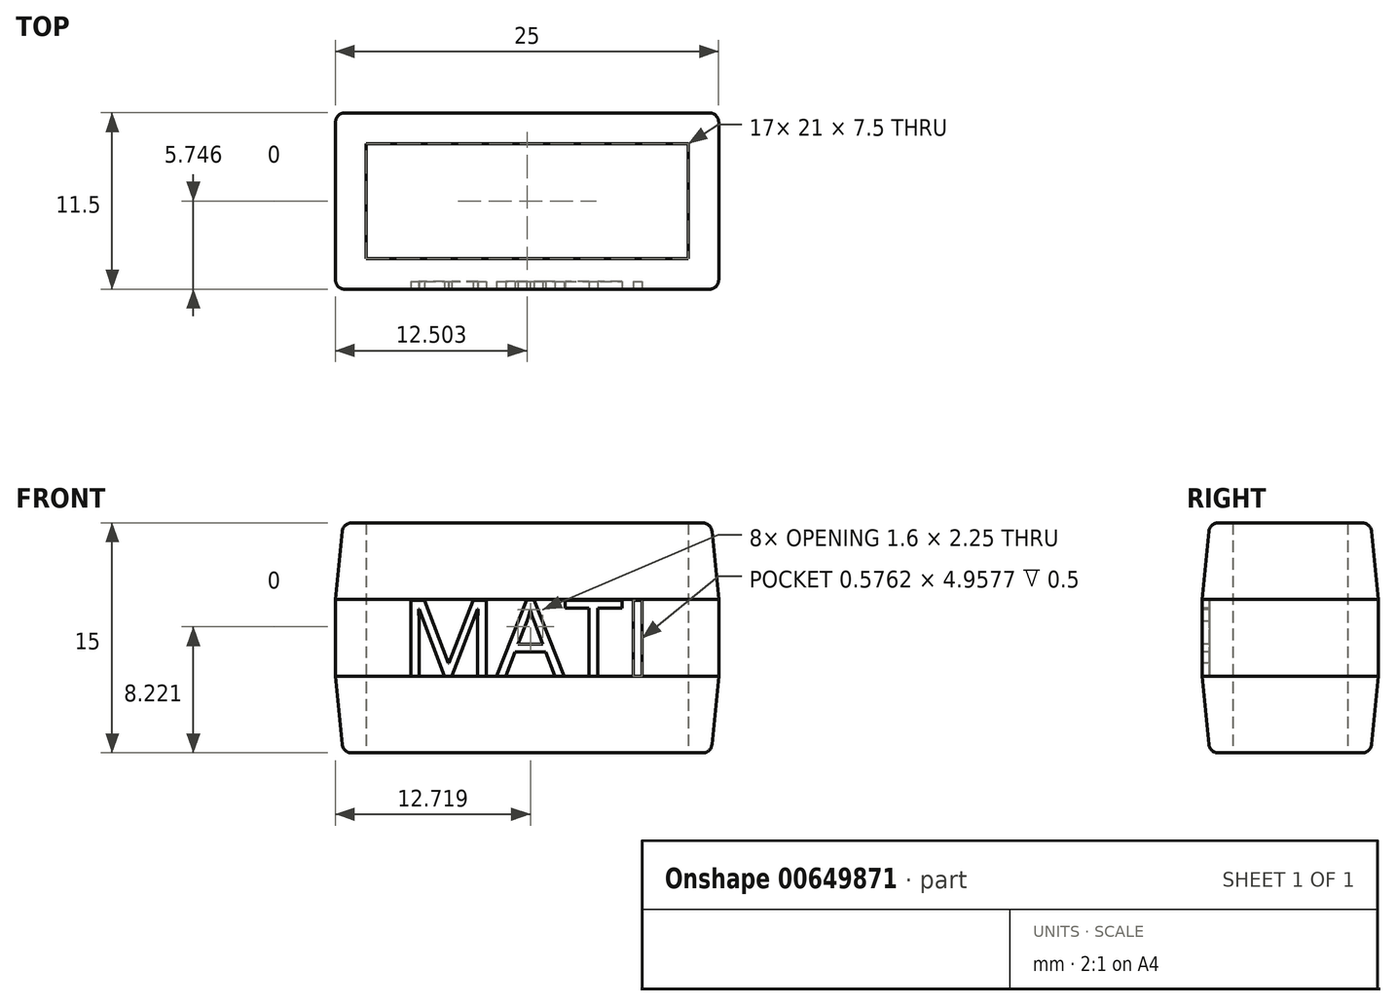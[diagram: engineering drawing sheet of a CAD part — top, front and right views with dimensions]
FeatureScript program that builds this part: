
annotation { "Feature Type Name" : "Feature", "Feature Type Description" : "" }
export const myFeature = defineFeature(function(context is Context, id is Id, definition is map)
    precondition{}
    {
        {
            var Q0;
            Q0=qCreatedBy(makeId("Top.planeOp"),FACE);
            var sketch = newSketch(context, id + "F0", { "sketchPlane" : qUnion([Q0])});
            skLineSegment(sketch, "E0.bottom", {"start": v(-10.05, 2.82) * mm, "end": v(10.95, 2.82) * mm});
            skLineSegment(sketch, "E0.top", {"start": v(-10.05, -4.68) * mm, "end": v(10.95, -4.68) * mm});
            skLineSegment(sketch, "E0.left", {"start": v(-10.05, 2.82) * mm, "end": v(-10.05, -4.68) * mm});
            skLineSegment(sketch, "E0.right", {"start": v(10.95, 2.82) * mm, "end": v(10.95, -4.68) * mm});
            skLineSegment(sketch, "E1", {"start": v(-19.72, 0) * mm, "end": v(20.77, 0) * mm, "construction": true});
            skLineSegment(sketch, "E2", {"start": v(0, 18.73) * mm, "end": v(0, -21.6) * mm, "construction": true});
            skLineSegment(sketch, "E3.0", {"start": v(-12.05, 4.82) * mm, "end": v(12.95, 4.82) * mm});
            skLineSegment(sketch, "E3.1", {"start": v(-12.05, 4.82) * mm, "end": v(-12.05, -6.68) * mm});
            skLineSegment(sketch, "E3.2", {"start": v(-12.05, -6.68) * mm, "end": v(12.95, -6.68) * mm});
            skLineSegment(sketch, "E3.3", {"start": v(12.95, 4.82) * mm, "end": v(12.95, -6.68) * mm});
            skSolve(sketch);
        }
        {
            var Q0;
            Q0=makeQuery(id+"F0.imprint","IMPRINT",FACE,{"disambiguationData":[TD([[makeQuery(id+"F0.imprint","IMPRINT",EDGE,{"derivedFrom":sQuery(id+"F0.wireOp",EDGE,"E0.bottom")}),1.0]])]});
            extrude(context, id + "F1", {"entities" : qUnion([Q0]), "depth" : 15 * mm, "offsetDistance" : 25 * mm});
        }
        {
            var Q0;
            Q0=makeQuery(id+"F1.opExtrude","CAP_EDGE",EDGE,{"disambiguationData":[OSD([sQuery(id+"F0.wireOp",EDGE,"E3.0")])],"isStart":false});
            var Q1;
            Q1=makeQuery(id+"F1.opExtrude","CAP_EDGE",EDGE,{"disambiguationData":[OSD([sQuery(id+"F0.wireOp",EDGE,"E3.3")])],"isStart":false});
            var Q2;
            Q2=makeQuery(id+"F1.opExtrude","CAP_EDGE",EDGE,{"disambiguationData":[OSD([sQuery(id+"F0.wireOp",EDGE,"E3.2")])],"isStart":false});
            var Q3;
            Q3=makeQuery(id+"F1.opExtrude","CAP_EDGE",EDGE,{"disambiguationData":[OSD([sQuery(id+"F0.wireOp",EDGE,"E3.1")])],"isStart":false});
            chamfer(context, id + "F2", {"entities" : qUnion([Q0, Q1, Q2, Q3]), "chamferType" : ChamferType.TWO_OFFSETS, "width1" : 5 * mm, "oppositeDirection" : false, "width2" : 0.5 * mm, "tangentPropagation" : true});
        }
        {
            var Q0;
            Q0=makeQuery(id+"F1.opExtrude","CAP_EDGE",EDGE,{"disambiguationData":[OSD([sQuery(id+"F0.wireOp",EDGE,"E3.3")])],"isStart":true});
            var Q1;
            Q1=makeQuery(id+"F1.opExtrude","CAP_EDGE",EDGE,{"disambiguationData":[OSD([sQuery(id+"F0.wireOp",EDGE,"E3.0")])],"isStart":true});
            var Q2;
            Q2=makeQuery(id+"F1.opExtrude","CAP_EDGE",EDGE,{"disambiguationData":[OSD([sQuery(id+"F0.wireOp",EDGE,"E3.1")])],"isStart":true});
            var Q3;
            Q3=makeQuery(id+"F1.opExtrude","CAP_EDGE",EDGE,{"disambiguationData":[OSD([sQuery(id+"F0.wireOp",EDGE,"E3.2")])],"isStart":true});
            chamfer(context, id + "F3", {"entities" : qUnion([Q0, Q1, Q2, Q3]), "chamferType" : ChamferType.TWO_OFFSETS, "width1" : 5 * mm, "oppositeDirection" : true, "width2" : 0.5 * mm, "tangentPropagation" : true});
        }
        {
            var Q0;
            {var subQ0=sQuery(id+"F0.wireOp",EDGE,"E3.0");Q0=makeQuery(id+"F2.opChamfer","BLEND_EDGE",EDGE,{"blendedFrom":[makeQuery(id+"F1.opExtrude","CAP_EDGE",EDGE,{"disambiguationData":[OSD([subQ0])],"isStart":false}),makeQuery(id+"F1.opExtrude","CAP_FACE",FACE,{"disambiguationData":[OSD([sQuery(id+"F0.wireOp",EDGE,"E0.bottom"),sQuery(id+"F0.wireOp",EDGE,"E0.top"),sQuery(id+"F0.wireOp",EDGE,"E0.left"),sQuery(id+"F0.wireOp",EDGE,"E0.right"),subQ0,sQuery(id+"F0.wireOp",EDGE,"E3.1"),sQuery(id+"F0.wireOp",EDGE,"E3.2"),sQuery(id+"F0.wireOp",EDGE,"E3.3")])],"isStart":false})],"blendedInto":[makeQuery(id+"F1.opExtrude","CAP_FACE",FACE,{"disambiguationData":[OSD([sQuery(id+"F0.wireOp",EDGE,"E0.bottom"),sQuery(id+"F0.wireOp",EDGE,"E0.top"),sQuery(id+"F0.wireOp",EDGE,"E0.left"),sQuery(id+"F0.wireOp",EDGE,"E0.right"),subQ0,sQuery(id+"F0.wireOp",EDGE,"E3.1"),sQuery(id+"F0.wireOp",EDGE,"E3.2"),sQuery(id+"F0.wireOp",EDGE,"E3.3")])],"isStart":false})]});}
            var Q1;
            {var subQ0=sQuery(id+"F0.wireOp",EDGE,"E3.3");Q1=makeQuery(id+"F2.opChamfer","BLEND_EDGE",EDGE,{"blendedFrom":[makeQuery(id+"F1.opExtrude","CAP_EDGE",EDGE,{"disambiguationData":[OSD([subQ0])],"isStart":false}),makeQuery(id+"F1.opExtrude","CAP_FACE",FACE,{"disambiguationData":[OSD([sQuery(id+"F0.wireOp",EDGE,"E0.bottom"),sQuery(id+"F0.wireOp",EDGE,"E0.top"),sQuery(id+"F0.wireOp",EDGE,"E0.left"),sQuery(id+"F0.wireOp",EDGE,"E0.right"),sQuery(id+"F0.wireOp",EDGE,"E3.0"),sQuery(id+"F0.wireOp",EDGE,"E3.1"),sQuery(id+"F0.wireOp",EDGE,"E3.2"),subQ0])],"isStart":false})],"blendedInto":[makeQuery(id+"F1.opExtrude","CAP_FACE",FACE,{"disambiguationData":[OSD([sQuery(id+"F0.wireOp",EDGE,"E0.bottom"),sQuery(id+"F0.wireOp",EDGE,"E0.top"),sQuery(id+"F0.wireOp",EDGE,"E0.left"),sQuery(id+"F0.wireOp",EDGE,"E0.right"),sQuery(id+"F0.wireOp",EDGE,"E3.0"),sQuery(id+"F0.wireOp",EDGE,"E3.1"),sQuery(id+"F0.wireOp",EDGE,"E3.2"),subQ0])],"isStart":false})]});}
            var Q2;
            {var subQ0=sQuery(id+"F0.wireOp",EDGE,"E3.2");Q2=makeQuery(id+"F2.opChamfer","BLEND_EDGE",EDGE,{"blendedFrom":[makeQuery(id+"F1.opExtrude","CAP_EDGE",EDGE,{"disambiguationData":[OSD([subQ0])],"isStart":false}),makeQuery(id+"F1.opExtrude","CAP_FACE",FACE,{"disambiguationData":[OSD([sQuery(id+"F0.wireOp",EDGE,"E0.bottom"),sQuery(id+"F0.wireOp",EDGE,"E0.top"),sQuery(id+"F0.wireOp",EDGE,"E0.left"),sQuery(id+"F0.wireOp",EDGE,"E0.right"),sQuery(id+"F0.wireOp",EDGE,"E3.0"),sQuery(id+"F0.wireOp",EDGE,"E3.1"),subQ0,sQuery(id+"F0.wireOp",EDGE,"E3.3")])],"isStart":false})],"blendedInto":[makeQuery(id+"F1.opExtrude","CAP_FACE",FACE,{"disambiguationData":[OSD([sQuery(id+"F0.wireOp",EDGE,"E0.bottom"),sQuery(id+"F0.wireOp",EDGE,"E0.top"),sQuery(id+"F0.wireOp",EDGE,"E0.left"),sQuery(id+"F0.wireOp",EDGE,"E0.right"),sQuery(id+"F0.wireOp",EDGE,"E3.0"),sQuery(id+"F0.wireOp",EDGE,"E3.1"),subQ0,sQuery(id+"F0.wireOp",EDGE,"E3.3")])],"isStart":false})]});}
            var Q3;
            {var subQ0=sQuery(id+"F0.wireOp",EDGE,"E3.1");Q3=makeQuery(id+"F2.opChamfer","BLEND_EDGE",EDGE,{"blendedFrom":[makeQuery(id+"F1.opExtrude","CAP_EDGE",EDGE,{"disambiguationData":[OSD([subQ0])],"isStart":false}),makeQuery(id+"F1.opExtrude","CAP_FACE",FACE,{"disambiguationData":[OSD([sQuery(id+"F0.wireOp",EDGE,"E0.bottom"),sQuery(id+"F0.wireOp",EDGE,"E0.top"),sQuery(id+"F0.wireOp",EDGE,"E0.left"),sQuery(id+"F0.wireOp",EDGE,"E0.right"),sQuery(id+"F0.wireOp",EDGE,"E3.0"),subQ0,sQuery(id+"F0.wireOp",EDGE,"E3.2"),sQuery(id+"F0.wireOp",EDGE,"E3.3")])],"isStart":false})],"blendedInto":[makeQuery(id+"F1.opExtrude","CAP_FACE",FACE,{"disambiguationData":[OSD([sQuery(id+"F0.wireOp",EDGE,"E0.bottom"),sQuery(id+"F0.wireOp",EDGE,"E0.top"),sQuery(id+"F0.wireOp",EDGE,"E0.left"),sQuery(id+"F0.wireOp",EDGE,"E0.right"),sQuery(id+"F0.wireOp",EDGE,"E3.0"),subQ0,sQuery(id+"F0.wireOp",EDGE,"E3.2"),sQuery(id+"F0.wireOp",EDGE,"E3.3")])],"isStart":false})]});}
            var Q4;
            Q4=makeQuery(id+"F2.opChamfer","BLEND_EDGE",EDGE,{"blendedFrom":[makeQuery(id+"F1.opExtrude","CAP_EDGE",EDGE,{"disambiguationData":[OSD([sQuery(id+"F0.wireOp",EDGE,"E3.1")])],"isStart":false}),makeQuery(id+"F1.opExtrude","CAP_EDGE",EDGE,{"disambiguationData":[OSD([sQuery(id+"F0.wireOp",EDGE,"E3.2")])],"isStart":false})],"blendedInto":[]});
            var Q5;
            Q5=makeQuery(id+"F1.opExtrude","SWEPT_EDGE",EDGE,{"disambiguationData":[OSD([sQuery(id+"F0.wireOp",EDGE,"E3.1"),sQuery(id+"F0.wireOp",EDGE,"E3.2")])]});
            var Q6;
            Q6=makeQuery(id+"F3.opChamfer","BLEND_EDGE",EDGE,{"blendedFrom":[makeQuery(id+"F1.opExtrude","CAP_EDGE",EDGE,{"disambiguationData":[OSD([sQuery(id+"F0.wireOp",EDGE,"E3.1")])],"isStart":true}),makeQuery(id+"F1.opExtrude","CAP_EDGE",EDGE,{"disambiguationData":[OSD([sQuery(id+"F0.wireOp",EDGE,"E3.2")])],"isStart":true})],"blendedInto":[]});
            var Q7;
            Q7=makeQuery(id+"F2.opChamfer","BLEND_EDGE",EDGE,{"blendedFrom":[makeQuery(id+"F1.opExtrude","CAP_EDGE",EDGE,{"disambiguationData":[OSD([sQuery(id+"F0.wireOp",EDGE,"E3.2")])],"isStart":false}),makeQuery(id+"F1.opExtrude","CAP_EDGE",EDGE,{"disambiguationData":[OSD([sQuery(id+"F0.wireOp",EDGE,"E3.3")])],"isStart":false})],"blendedInto":[]});
            var Q8;
            Q8=makeQuery(id+"F1.opExtrude","SWEPT_EDGE",EDGE,{"disambiguationData":[OSD([sQuery(id+"F0.wireOp",EDGE,"E3.2"),sQuery(id+"F0.wireOp",EDGE,"E3.3")])]});
            var Q9;
            Q9=makeQuery(id+"F3.opChamfer","BLEND_EDGE",EDGE,{"blendedFrom":[makeQuery(id+"F1.opExtrude","CAP_EDGE",EDGE,{"disambiguationData":[OSD([sQuery(id+"F0.wireOp",EDGE,"E3.2")])],"isStart":true}),makeQuery(id+"F1.opExtrude","CAP_EDGE",EDGE,{"disambiguationData":[OSD([sQuery(id+"F0.wireOp",EDGE,"E3.3")])],"isStart":true})],"blendedInto":[]});
            var Q10;
            Q10=makeQuery(id+"F2.opChamfer","BLEND_EDGE",EDGE,{"blendedFrom":[makeQuery(id+"F1.opExtrude","CAP_EDGE",EDGE,{"disambiguationData":[OSD([sQuery(id+"F0.wireOp",EDGE,"E3.0")])],"isStart":false}),makeQuery(id+"F1.opExtrude","CAP_EDGE",EDGE,{"disambiguationData":[OSD([sQuery(id+"F0.wireOp",EDGE,"E3.3")])],"isStart":false})],"blendedInto":[]});
            var Q11;
            Q11=makeQuery(id+"F1.opExtrude","SWEPT_EDGE",EDGE,{"disambiguationData":[OSD([sQuery(id+"F0.wireOp",EDGE,"E3.0"),sQuery(id+"F0.wireOp",EDGE,"E3.3")])]});
            var Q12;
            Q12=makeQuery(id+"F3.opChamfer","BLEND_EDGE",EDGE,{"blendedFrom":[makeQuery(id+"F1.opExtrude","CAP_EDGE",EDGE,{"disambiguationData":[OSD([sQuery(id+"F0.wireOp",EDGE,"E3.0")])],"isStart":true}),makeQuery(id+"F1.opExtrude","CAP_EDGE",EDGE,{"disambiguationData":[OSD([sQuery(id+"F0.wireOp",EDGE,"E3.3")])],"isStart":true})],"blendedInto":[]});
            var Q13;
            Q13=makeQuery(id+"F2.opChamfer","BLEND_EDGE",EDGE,{"blendedFrom":[makeQuery(id+"F1.opExtrude","CAP_EDGE",EDGE,{"disambiguationData":[OSD([sQuery(id+"F0.wireOp",EDGE,"E3.0")])],"isStart":false}),makeQuery(id+"F1.opExtrude","CAP_EDGE",EDGE,{"disambiguationData":[OSD([sQuery(id+"F0.wireOp",EDGE,"E3.1")])],"isStart":false})],"blendedInto":[]});
            var Q14;
            Q14=makeQuery(id+"F1.opExtrude","SWEPT_EDGE",EDGE,{"disambiguationData":[OSD([sQuery(id+"F0.wireOp",EDGE,"E3.0"),sQuery(id+"F0.wireOp",EDGE,"E3.1")])]});
            var Q15;
            Q15=makeQuery(id+"F3.opChamfer","BLEND_EDGE",EDGE,{"blendedFrom":[makeQuery(id+"F1.opExtrude","CAP_EDGE",EDGE,{"disambiguationData":[OSD([sQuery(id+"F0.wireOp",EDGE,"E3.0")])],"isStart":true}),makeQuery(id+"F1.opExtrude","CAP_EDGE",EDGE,{"disambiguationData":[OSD([sQuery(id+"F0.wireOp",EDGE,"E3.1")])],"isStart":true})],"blendedInto":[]});
            var Q16;
            {var subQ0=sQuery(id+"F0.wireOp",EDGE,"E3.0");Q16=makeQuery(id+"F3.opChamfer","BLEND_EDGE",EDGE,{"blendedFrom":[makeQuery(id+"F1.opExtrude","CAP_EDGE",EDGE,{"disambiguationData":[OSD([subQ0])],"isStart":true}),makeQuery(id+"F1.opExtrude","CAP_FACE",FACE,{"disambiguationData":[OSD([sQuery(id+"F0.wireOp",EDGE,"E0.bottom"),sQuery(id+"F0.wireOp",EDGE,"E0.top"),sQuery(id+"F0.wireOp",EDGE,"E0.left"),sQuery(id+"F0.wireOp",EDGE,"E0.right"),subQ0,sQuery(id+"F0.wireOp",EDGE,"E3.1"),sQuery(id+"F0.wireOp",EDGE,"E3.2"),sQuery(id+"F0.wireOp",EDGE,"E3.3")])],"isStart":true})],"blendedInto":[makeQuery(id+"F1.opExtrude","CAP_FACE",FACE,{"disambiguationData":[OSD([sQuery(id+"F0.wireOp",EDGE,"E0.bottom"),sQuery(id+"F0.wireOp",EDGE,"E0.top"),sQuery(id+"F0.wireOp",EDGE,"E0.left"),sQuery(id+"F0.wireOp",EDGE,"E0.right"),subQ0,sQuery(id+"F0.wireOp",EDGE,"E3.1"),sQuery(id+"F0.wireOp",EDGE,"E3.2"),sQuery(id+"F0.wireOp",EDGE,"E3.3")])],"isStart":true})]});}
            var Q17;
            {var subQ0=sQuery(id+"F0.wireOp",EDGE,"E3.3");Q17=makeQuery(id+"F3.opChamfer","BLEND_EDGE",EDGE,{"blendedFrom":[makeQuery(id+"F1.opExtrude","CAP_EDGE",EDGE,{"disambiguationData":[OSD([subQ0])],"isStart":true}),makeQuery(id+"F1.opExtrude","CAP_FACE",FACE,{"disambiguationData":[OSD([sQuery(id+"F0.wireOp",EDGE,"E0.bottom"),sQuery(id+"F0.wireOp",EDGE,"E0.top"),sQuery(id+"F0.wireOp",EDGE,"E0.left"),sQuery(id+"F0.wireOp",EDGE,"E0.right"),sQuery(id+"F0.wireOp",EDGE,"E3.0"),sQuery(id+"F0.wireOp",EDGE,"E3.1"),sQuery(id+"F0.wireOp",EDGE,"E3.2"),subQ0])],"isStart":true})],"blendedInto":[makeQuery(id+"F1.opExtrude","CAP_FACE",FACE,{"disambiguationData":[OSD([sQuery(id+"F0.wireOp",EDGE,"E0.bottom"),sQuery(id+"F0.wireOp",EDGE,"E0.top"),sQuery(id+"F0.wireOp",EDGE,"E0.left"),sQuery(id+"F0.wireOp",EDGE,"E0.right"),sQuery(id+"F0.wireOp",EDGE,"E3.0"),sQuery(id+"F0.wireOp",EDGE,"E3.1"),sQuery(id+"F0.wireOp",EDGE,"E3.2"),subQ0])],"isStart":true})]});}
            var Q18;
            {var subQ0=sQuery(id+"F0.wireOp",EDGE,"E3.2");Q18=makeQuery(id+"F3.opChamfer","BLEND_EDGE",EDGE,{"blendedFrom":[makeQuery(id+"F1.opExtrude","CAP_EDGE",EDGE,{"disambiguationData":[OSD([subQ0])],"isStart":true}),makeQuery(id+"F1.opExtrude","CAP_FACE",FACE,{"disambiguationData":[OSD([sQuery(id+"F0.wireOp",EDGE,"E0.bottom"),sQuery(id+"F0.wireOp",EDGE,"E0.top"),sQuery(id+"F0.wireOp",EDGE,"E0.left"),sQuery(id+"F0.wireOp",EDGE,"E0.right"),sQuery(id+"F0.wireOp",EDGE,"E3.0"),sQuery(id+"F0.wireOp",EDGE,"E3.1"),subQ0,sQuery(id+"F0.wireOp",EDGE,"E3.3")])],"isStart":true})],"blendedInto":[makeQuery(id+"F1.opExtrude","CAP_FACE",FACE,{"disambiguationData":[OSD([sQuery(id+"F0.wireOp",EDGE,"E0.bottom"),sQuery(id+"F0.wireOp",EDGE,"E0.top"),sQuery(id+"F0.wireOp",EDGE,"E0.left"),sQuery(id+"F0.wireOp",EDGE,"E0.right"),sQuery(id+"F0.wireOp",EDGE,"E3.0"),sQuery(id+"F0.wireOp",EDGE,"E3.1"),subQ0,sQuery(id+"F0.wireOp",EDGE,"E3.3")])],"isStart":true})]});}
            var Q19;
            {var subQ0=sQuery(id+"F0.wireOp",EDGE,"E3.1");Q19=makeQuery(id+"F3.opChamfer","BLEND_EDGE",EDGE,{"blendedFrom":[makeQuery(id+"F1.opExtrude","CAP_EDGE",EDGE,{"disambiguationData":[OSD([subQ0])],"isStart":true}),makeQuery(id+"F1.opExtrude","CAP_FACE",FACE,{"disambiguationData":[OSD([sQuery(id+"F0.wireOp",EDGE,"E0.bottom"),sQuery(id+"F0.wireOp",EDGE,"E0.top"),sQuery(id+"F0.wireOp",EDGE,"E0.left"),sQuery(id+"F0.wireOp",EDGE,"E0.right"),sQuery(id+"F0.wireOp",EDGE,"E3.0"),subQ0,sQuery(id+"F0.wireOp",EDGE,"E3.2"),sQuery(id+"F0.wireOp",EDGE,"E3.3")])],"isStart":true})],"blendedInto":[makeQuery(id+"F1.opExtrude","CAP_FACE",FACE,{"disambiguationData":[OSD([sQuery(id+"F0.wireOp",EDGE,"E0.bottom"),sQuery(id+"F0.wireOp",EDGE,"E0.top"),sQuery(id+"F0.wireOp",EDGE,"E0.left"),sQuery(id+"F0.wireOp",EDGE,"E0.right"),sQuery(id+"F0.wireOp",EDGE,"E3.0"),subQ0,sQuery(id+"F0.wireOp",EDGE,"E3.2"),sQuery(id+"F0.wireOp",EDGE,"E3.3")])],"isStart":true})]});}
            fillet(context, id + "F4", {"entities" : qUnion([Q0, Q1, Q2, Q3, Q4, Q5, Q6, Q7, Q8, Q9, Q10, Q11, Q12, Q13, Q14, Q15, Q16, Q17, Q18, Q19]), "radius" : .6 * mm, "tangentPropagation" : true, "allowEdgeOverflow" : false});
        }
        {
            var Q0;
            Q0=makeQuery(id+"F1.opExtrude","SWEPT_FACE",FACE,{"disambiguationData":[OSD([sQuery(id+"F0.wireOp",EDGE,"E3.2")])]});
            var sketch = newSketch(context, id + "F5", { "sketchPlane" : qUnion([Q0])});
            skText(sketch, "E4", { "text": "MATI", "fontName": "OpenSans-Regular.ttf"});
            const initialGuessF5  = {"E4": [-0.0078, 0.005, 1, 0, 0.005]};
            skSetInitialGuess(sketch, initialGuessF5);
            skSolve(sketch);
        }
        {
            var Q0;
            Q0 = qSketchRegion(id + "F5", true);
            extrude(context, id + "F6", {"entities" : qUnion([Q0]), "operationType" : NewBodyOperationType.REMOVE, "oppositeDirection" : true, "depth" : .5 * mm, "offsetDistance" : 25 * mm});
        }
    });
